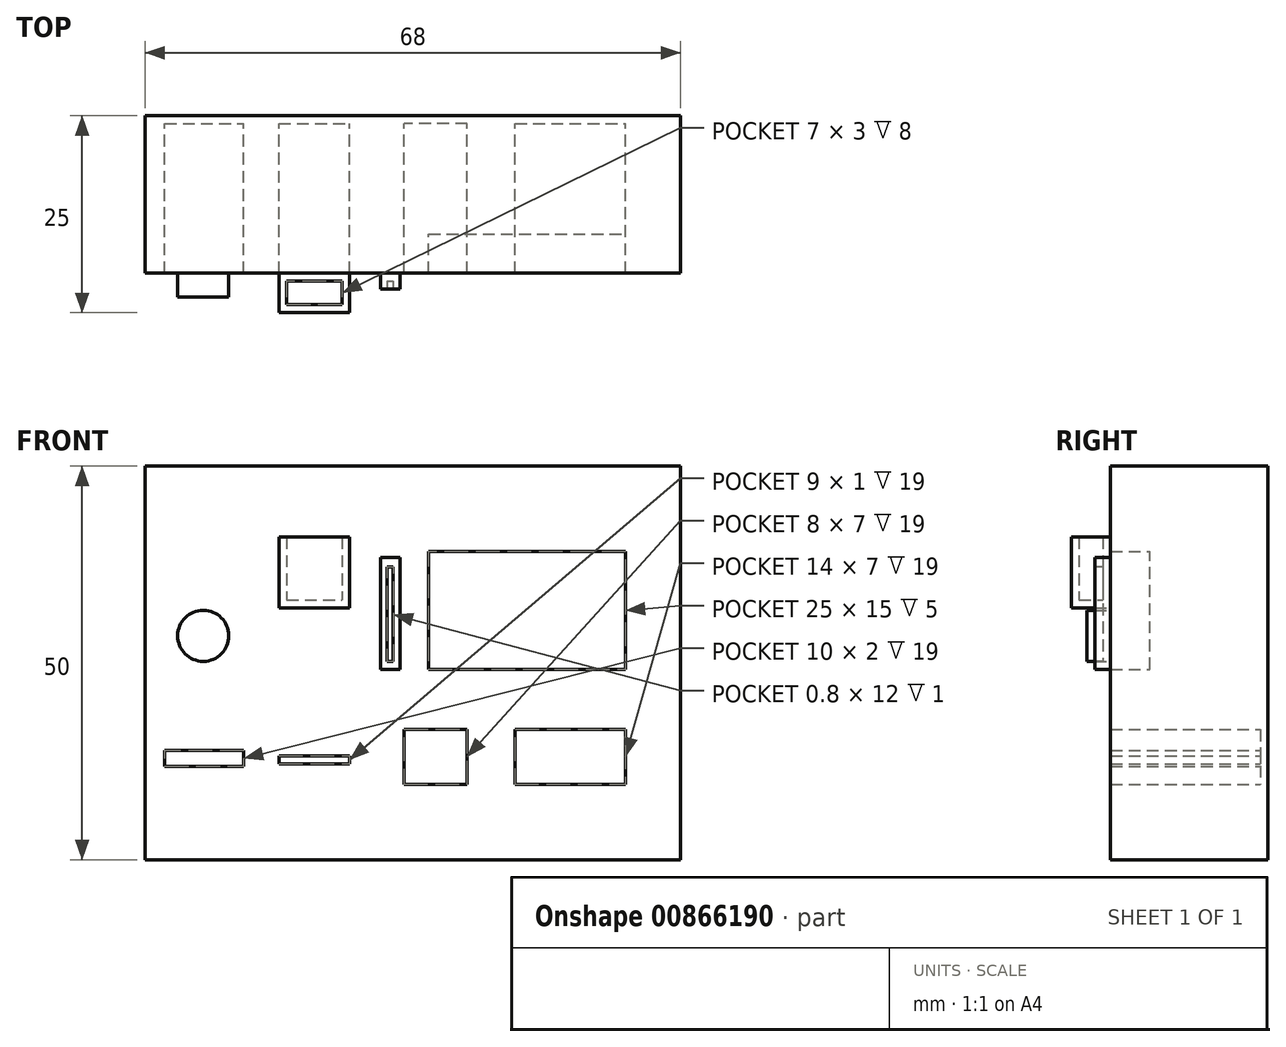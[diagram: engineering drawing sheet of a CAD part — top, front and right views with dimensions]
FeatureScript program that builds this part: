
annotation { "Feature Type Name" : "Feature", "Feature Type Description" : "" }
export const myFeature = defineFeature(function(context is Context, id is Id, definition is map)
    precondition{}
    {
        {
            var Q0;
            Q0=qCreatedBy(makeId("Front.planeOp"),FACE);
            var sketch = newSketch(context, id + "F0", { "sketchPlane" : qUnion([Q0])});
            skLineSegment(sketch, "E0.bottom", {"start": v(-51.91, 14.88) * mm, "end": v(-36.91, 14.88) * mm});
            skLineSegment(sketch, "E0.top", {"start": v(-51.91, -35.12) * mm, "end": v(-36.91, -35.12) * mm});
            skLineSegment(sketch, "E0.left", {"start": v(-51.91, 14.88) * mm, "end": v(-51.91, -35.12) * mm});
            skLineSegment(sketch, "E0.right", {"start": v(-36.91, 14.88) * mm, "end": v(-36.91, -35.12) * mm});
            skLineSegment(sketch, "E1.bottom", {"start": v(-36.91, 14.88) * mm, "end": v(-23.91, 14.88) * mm});
            skLineSegment(sketch, "E1.top", {"start": v(-36.91, -35.12) * mm, "end": v(-23.91, -35.12) * mm});
            skLineSegment(sketch, "E1.right", {"start": v(-23.91, 14.88) * mm, "end": v(-23.91, -35.12) * mm});
            skLineSegment(sketch, "E2.bottom", {"start": v(-23.91, 14.88) * mm, "end": v(16.09, 14.88) * mm});
            skLineSegment(sketch, "E2.top", {"start": v(-23.91, -35.12) * mm, "end": v(16.09, -35.12) * mm});
            skLineSegment(sketch, "E2.right", {"start": v(16.09, 14.88) * mm, "end": v(16.09, -35.12) * mm});
            skSolve(sketch);
        }
        {
            var Q0;
            Q0=makeQuery(id+"F0.imprint","IMPRINT",FACE,{"disambiguationData":[TD([[makeQuery(id+"F0.imprint","IMPRINT",EDGE,{"derivedFrom":sQuery(id+"F0.wireOp",EDGE,"E0.bottom")}),-1.0]])]});
            extrude(context, id + "F1", {"entities" : qUnion([Q0]), "depth" : 20 * mm, "offsetDistance" : 25 * mm});
        }
        {
            var Q0;
            Q0=makeQuery(id+"F0.imprint","IMPRINT",FACE,{"disambiguationData":[TD([[makeQuery(id+"F0.imprint","IMPRINT",EDGE,{"derivedFrom":sQuery(id+"F0.wireOp",EDGE,"E1.bottom")}),-1.0]])]});
            extrude(context, id + "F2", {"entities" : qUnion([Q0]), "depth" : 20 * mm, "offsetDistance" : 25 * mm});
        }
        {
            var Q0;
            Q0=makeQuery(id+"F0.imprint","IMPRINT",FACE,{"disambiguationData":[TD([[makeQuery(id+"F0.imprint","IMPRINT",EDGE,{"derivedFrom":sQuery(id+"F0.wireOp",EDGE,"E2.bottom")}),-1.0]])]});
            extrude(context, id + "F3", {"entities" : qUnion([Q0]), "depth" : 20 * mm, "offsetDistance" : 25 * mm});
        }
        {
            var Q0;
            Q0=qCreatedBy(makeId("Front.planeOp"),FACE);
            var sketch = newSketch(context, id + "F4", { "sketchPlane" : qUnion([Q0])});
            skLineSegment(sketch, "E3.bottom", {"start": v(-49.41, -21.26) * mm, "end": v(-39.41, -21.26) * mm});
            skLineSegment(sketch, "E3.top", {"start": v(-49.41, -23.26) * mm, "end": v(-39.41, -23.26) * mm});
            skLineSegment(sketch, "E3.left", {"start": v(-49.41, -21.26) * mm, "end": v(-49.41, -23.26) * mm});
            skLineSegment(sketch, "E3.right", {"start": v(-39.41, -21.26) * mm, "end": v(-39.41, -23.26) * mm});
            skSolve(sketch);
        }
        {
            var Q0;
            Q0 = qSketchRegion(id + "F4", true);
            extrude(context, id + "F5", {"entities" : qUnion([Q0]), "operationType" : NewBodyOperationType.REMOVE, "depth" : 25 * mm, "offsetDistance" : 25 * mm});
        }
        {
            var Q0;
            Q0=qCreatedBy(makeId("Front.planeOp"),FACE);
            var sketch = newSketch(context, id + "F6", { "sketchPlane" : qUnion([Q0])});
            skLineSegment(sketch, "E4.bottom", {"start": v(-34.91, -21.95) * mm, "end": v(-25.91, -21.95) * mm});
            skLineSegment(sketch, "E4.top", {"start": v(-34.91, -22.95) * mm, "end": v(-25.91, -22.95) * mm});
            skLineSegment(sketch, "E4.left", {"start": v(-34.91, -21.95) * mm, "end": v(-34.91, -22.95) * mm});
            skLineSegment(sketch, "E4.right", {"start": v(-25.91, -21.95) * mm, "end": v(-25.91, -22.95) * mm});
            skSolve(sketch);
        }
        {
            var Q0;
            Q0 = qSketchRegion(id + "F6", true);
            extrude(context, id + "F7", {"entities" : qUnion([Q0]), "operationType" : NewBodyOperationType.REMOVE, "depth" : 25 * mm, "offsetDistance" : 25 * mm});
        }
        {
            var Q0;
            Q0=qCreatedBy(makeId("Front.planeOp"),FACE);
            var sketch = newSketch(context, id + "F8", { "sketchPlane" : qUnion([Q0])});
            skLineSegment(sketch, "E5.bottom", {"start": v(-4.91, -18.59) * mm, "end": v(9.09, -18.59) * mm});
            skLineSegment(sketch, "E5.top", {"start": v(-4.91, -25.59) * mm, "end": v(9.09, -25.59) * mm});
            skLineSegment(sketch, "E5.left", {"start": v(-4.91, -18.59) * mm, "end": v(-4.91, -25.59) * mm});
            skLineSegment(sketch, "E5.right", {"start": v(9.09, -18.59) * mm, "end": v(9.09, -25.59) * mm});
            skLineSegment(sketch, "E6.bottom", {"start": v(-11, -18.59) * mm, "end": v(-19, -18.59) * mm});
            skLineSegment(sketch, "E6.top", {"start": v(-11, -25.59) * mm, "end": v(-19, -25.59) * mm});
            skLineSegment(sketch, "E6.left", {"start": v(-11, -18.59) * mm, "end": v(-11, -25.59) * mm});
            skLineSegment(sketch, "E6.right", {"start": v(-19, -18.59) * mm, "end": v(-19, -25.59) * mm});
            skSolve(sketch);
        }
        {
            var Q0;
            Q0 = qSketchRegion(id + "F8", true);
            extrude(context, id + "F9", {"entities" : qUnion([Q0]), "operationType" : NewBodyOperationType.REMOVE, "depth" : 25 * mm, "offsetDistance" : 25 * mm});
        }
        {
            var Q0;
            Q0=qCreatedBy(makeId("Front.planeOp"),FACE);
            cPlane(context, id + "F10", {"entities" : qUnion([Q0]), "cplaneType" : CPlaneType.OFFSET, "offset" : 15 * mm, "width" : 150 * mm, "height" : 150 * mm});
        }
        {
            var Q0;
            Q0=qCreatedBy(id+"F10.planeOp",FACE);
            var sketch = newSketch(context, id + "F11", { "sketchPlane" : qUnion([Q0])});
            skLineSegment(sketch, "E7.bottom", {"start": v(-15.91, -10.94) * mm, "end": v(9.09, -10.94) * mm});
            skLineSegment(sketch, "E7.top", {"start": v(-15.91, 4.06) * mm, "end": v(9.09, 4.06) * mm});
            skLineSegment(sketch, "E7.left", {"start": v(-15.91, -10.94) * mm, "end": v(-15.91, 4.06) * mm});
            skLineSegment(sketch, "E7.right", {"start": v(9.09, -10.94) * mm, "end": v(9.09, 4.06) * mm});
            skSolve(sketch);
        }
        {
            var Q0;
            Q0 = qSketchRegion(id + "F11", true);
            extrude(context, id + "F12", {"entities" : qUnion([Q0]), "operationType" : NewBodyOperationType.REMOVE, "depth" : 25 * mm, "offsetDistance" : 25 * mm});
        }
        {
            var Q0;
            Q0=qCreatedBy(makeId("Front.planeOp"),FACE);
            var sketch = newSketch(context, id + "F13", { "sketchPlane" : qUnion([Q0])});
            skLineSegment(sketch, "E8.bottom", {"start": v(-50.6, -16.46) * mm, "end": v(13.57, -16.46) * mm});
            skLineSegment(sketch, "E8.top", {"start": v(-50.6, -28.68) * mm, "end": v(13.57, -28.68) * mm});
            skLineSegment(sketch, "E8.left", {"start": v(-50.6, -16.46) * mm, "end": v(-50.6, -28.68) * mm});
            skLineSegment(sketch, "E8.right", {"start": v(13.57, -16.46) * mm, "end": v(13.57, -28.68) * mm});
            skSolve(sketch);
        }
        {
            var Q0;
            Q0 = qSketchRegion(id + "F13", true);
            var Q1;
            Q1 = qConstructionFilter(qBodyType(qCreatedBy(id + "F13" ,EDGE), BodyType.WIRE), ConstructionObject.NO);
            extrude(context, id + "F14", {"entities" : qUnion([Q0]), "surfaceEntities" : qUnion([Q1]), "depth" : 1 * mm, "offsetDistance" : 25 * mm});
        }
        {
            var Q0;
            Q0=makeQuery(id+"F2.opExtrude","SWEPT_BODY",BODY,{"disambiguationData":[OSD([sQuery(id+"F0.wireOp",EDGE,"E1.bottom"),sQuery(id+"F0.wireOp",EDGE,"E1.top"),sQuery(id+"F0.wireOp",EDGE,"E0.right"),sQuery(id+"F0.wireOp",EDGE,"E1.right")])]});
            var Q1;
            Q1=makeQuery(id+"F3.opExtrude","SWEPT_BODY",BODY,{"disambiguationData":[OSD([sQuery(id+"F0.wireOp",EDGE,"E2.bottom"),sQuery(id+"F0.wireOp",EDGE,"E2.top"),sQuery(id+"F0.wireOp",EDGE,"E1.right"),sQuery(id+"F0.wireOp",EDGE,"E2.right")])]});
            var Q2;
            Q2=makeQuery(id+"F1.opExtrude","SWEPT_BODY",BODY,{"disambiguationData":[OSD([sQuery(id+"F0.wireOp",EDGE,"E0.bottom"),sQuery(id+"F0.wireOp",EDGE,"E0.top"),sQuery(id+"F0.wireOp",EDGE,"E0.left"),sQuery(id+"F0.wireOp",EDGE,"E0.right")])]});
            var Q3;
            Q3=makeQuery(id+"F14.opExtrude","SWEPT_BODY",BODY,{"disambiguationData":[OSD([sQuery(id+"F13.wireOp",EDGE,"E8.bottom"),sQuery(id+"F13.wireOp",EDGE,"E8.top"),sQuery(id+"F13.wireOp",EDGE,"E8.left"),sQuery(id+"F13.wireOp",EDGE,"E8.right")])]});
            booleanBodies(context, id + "F15", {"operationType" : BooleanOperationType.UNION, "tools" : qUnion([Q0, Q1, Q2, Q3])});
        }
        {
            var Q0;
            {var subQ0=sQuery(id+"F0.wireOp",EDGE,"E1.right");var subQ1=sQuery(id+"F0.wireOp",EDGE,"E0.right");Q0=makeQuery(id+"F15.opBoolean","MERGE",FACE,{"derivedFrom":[makeQuery(id+"F1.opExtrude","CAP_FACE",FACE,{"disambiguationData":[OSD([sQuery(id+"F0.wireOp",EDGE,"E0.bottom"),sQuery(id+"F0.wireOp",EDGE,"E0.top"),sQuery(id+"F0.wireOp",EDGE,"E0.left"),subQ1])],"isStart":false}),makeQuery(id+"F2.opExtrude","CAP_FACE",FACE,{"disambiguationData":[OSD([sQuery(id+"F0.wireOp",EDGE,"E1.bottom"),sQuery(id+"F0.wireOp",EDGE,"E1.top"),subQ1,subQ0])],"isStart":false}),makeQuery(id+"F3.opExtrude","CAP_FACE",FACE,{"disambiguationData":[OSD([sQuery(id+"F0.wireOp",EDGE,"E2.bottom"),sQuery(id+"F0.wireOp",EDGE,"E2.top"),subQ0,sQuery(id+"F0.wireOp",EDGE,"E2.right")])],"isStart":false})]});}
            var sketch = newSketch(context, id + "F16", { "sketchPlane" : qUnion([Q0])});
            skLineSegment(sketch, "E9.bottom", {"start": v(-34.91, 5.85) * mm, "end": v(-25.91, 5.85) * mm});
            skLineSegment(sketch, "E9.top", {"start": v(-34.91, -3.15) * mm, "end": v(-25.91, -3.15) * mm});
            skLineSegment(sketch, "E9.left", {"start": v(-34.91, 5.85) * mm, "end": v(-34.91, -3.15) * mm});
            skLineSegment(sketch, "E9.right", {"start": v(-25.91, 5.85) * mm, "end": v(-25.91, -3.15) * mm});
            skSolve(sketch);
        }
        {
            var Q0;
            Q0=makeQuery(id+"F16.imprint","IMPRINT",FACE,{"disambiguationData":[TD([[makeQuery(id+"F16.imprint","IMPRINT",EDGE,{"derivedFrom":sQuery(id+"F16.wireOp",EDGE,"E9.bottom")}),-1.0]])]});
            extrude(context, id + "F17", {"entities" : qUnion([Q0]), "depth" : 5 * mm, "offsetDistance" : 25 * mm});
        }
        {
            var Q0;
            Q0=makeQuery(id+"F17.opExtrude","SWEPT_FACE",FACE,{"disambiguationData":[OSD([sQuery(id+"F16.wireOp",EDGE,"E9.bottom")])]});
            shell(context, id + "F18", {"entities" : qUnion([Q0]), "thickness" : 1 * mm});
        }
        {
            var Q0;
            {var subQ0=sQuery(id+"F0.wireOp",EDGE,"E1.right");var subQ1=sQuery(id+"F0.wireOp",EDGE,"E0.right");Q0=makeQuery(id+"F15.opBoolean","MERGE",FACE,{"derivedFrom":[makeQuery(id+"F1.opExtrude","CAP_FACE",FACE,{"disambiguationData":[OSD([sQuery(id+"F0.wireOp",EDGE,"E0.bottom"),sQuery(id+"F0.wireOp",EDGE,"E0.top"),sQuery(id+"F0.wireOp",EDGE,"E0.left"),subQ1])],"isStart":false}),makeQuery(id+"F2.opExtrude","CAP_FACE",FACE,{"disambiguationData":[OSD([sQuery(id+"F0.wireOp",EDGE,"E1.bottom"),sQuery(id+"F0.wireOp",EDGE,"E1.top"),subQ1,subQ0])],"isStart":false}),makeQuery(id+"F3.opExtrude","CAP_FACE",FACE,{"disambiguationData":[OSD([sQuery(id+"F0.wireOp",EDGE,"E2.bottom"),sQuery(id+"F0.wireOp",EDGE,"E2.top"),subQ0,sQuery(id+"F0.wireOp",EDGE,"E2.right")])],"isStart":false})]});}
            var sketch = newSketch(context, id + "F19", { "sketchPlane" : qUnion([Q0])});
            skCircle(sketch, "E10", {"center": v(-44.52, -6.68) * mm, "radius": 3.24 * mm});
            skSolve(sketch);
        }
        {
            var Q0;
            Q0=makeQuery(id+"F19.imprint","IMPRINT",FACE,{"disambiguationData":[TD([[makeQuery(id+"F19.imprint","IMPRINT",EDGE,{"derivedFrom":sQuery(id+"F19.wireOp",EDGE,"E10")}),1.0]])]});
            extrude(context, id + "F20", {"entities" : qUnion([Q0]), "depth" : 3 * mm, "offsetDistance" : 25 * mm});
        }
        {
            var Q0;
            {var subQ0=sQuery(id+"F0.wireOp",EDGE,"E1.right");var subQ1=sQuery(id+"F0.wireOp",EDGE,"E0.right");Q0=makeQuery(id+"F15.opBoolean","MERGE",FACE,{"derivedFrom":[makeQuery(id+"F1.opExtrude","CAP_FACE",FACE,{"disambiguationData":[OSD([sQuery(id+"F0.wireOp",EDGE,"E0.bottom"),sQuery(id+"F0.wireOp",EDGE,"E0.top"),sQuery(id+"F0.wireOp",EDGE,"E0.left"),subQ1])],"isStart":false}),makeQuery(id+"F2.opExtrude","CAP_FACE",FACE,{"disambiguationData":[OSD([sQuery(id+"F0.wireOp",EDGE,"E1.bottom"),sQuery(id+"F0.wireOp",EDGE,"E1.top"),subQ1,subQ0])],"isStart":false}),makeQuery(id+"F3.opExtrude","CAP_FACE",FACE,{"disambiguationData":[OSD([sQuery(id+"F0.wireOp",EDGE,"E2.bottom"),sQuery(id+"F0.wireOp",EDGE,"E2.top"),subQ0,sQuery(id+"F0.wireOp",EDGE,"E2.right")])],"isStart":false})]});}
            var sketch = newSketch(context, id + "F21", { "sketchPlane" : qUnion([Q0])});
            skLineSegment(sketch, "E11.bottom", {"start": v(-22, 3.29) * mm, "end": v(-19.5, 3.29) * mm});
            skLineSegment(sketch, "E11.top", {"start": v(-22, -10.96) * mm, "end": v(-19.5, -10.96) * mm});
            skLineSegment(sketch, "E11.left", {"start": v(-22, 3.29) * mm, "end": v(-22, -10.96) * mm});
            skLineSegment(sketch, "E11.right", {"start": v(-19.5, 3.29) * mm, "end": v(-19.5, -10.96) * mm});
            skSolve(sketch);
        }
        {
            var Q0;
            Q0=makeQuery(id+"F21.imprint","IMPRINT",FACE,{"disambiguationData":[TD([[makeQuery(id+"F21.imprint","IMPRINT",EDGE,{"derivedFrom":sQuery(id+"F21.wireOp",EDGE,"E11.bottom")}),-1.0]])]});
            extrude(context, id + "F22", {"entities" : qUnion([Q0]), "operationType" : NewBodyOperationType.ADD, "depth" : 2 * mm, "offsetDistance" : 25 * mm});
        }
        {
            var Q0;
            Q0=makeQuery(id+"F22.opExtrude","CAP_FACE",FACE,{"disambiguationData":[OSD([sQuery(id+"F21.wireOp",EDGE,"E11.bottom"),sQuery(id+"F21.wireOp",EDGE,"E11.top"),sQuery(id+"F21.wireOp",EDGE,"E11.left"),sQuery(id+"F21.wireOp",EDGE,"E11.right")])],"isStart":false});
            var sketch = newSketch(context, id + "F23", { "sketchPlane" : qUnion([Q0])});
            skLineSegment(sketch, "E12.bottom", {"start": v(-21.18, 2.04) * mm, "end": v(-20.38, 2.04) * mm});
            skLineSegment(sketch, "E12.top", {"start": v(-21.18, -9.96) * mm, "end": v(-20.38, -9.96) * mm});
            skLineSegment(sketch, "E12.left", {"start": v(-21.18, 2.04) * mm, "end": v(-21.18, -9.96) * mm});
            skLineSegment(sketch, "E12.right", {"start": v(-20.38, 2.04) * mm, "end": v(-20.38, -9.96) * mm});
            skSolve(sketch);
        }
        {
            var Q0;
            Q0=makeQuery(id+"F23.imprint","IMPRINT",FACE,{"disambiguationData":[TD([[makeQuery(id+"F23.imprint","IMPRINT",EDGE,{"derivedFrom":sQuery(id+"F23.wireOp",EDGE,"E12.bottom")}),-1.0]])]});
            extrude(context, id + "F24", {"entities" : qUnion([Q0]), "operationType" : NewBodyOperationType.REMOVE, "oppositeDirection" : true, "depth" : 1 * mm, "offsetDistance" : 25 * mm});
        }
    });
